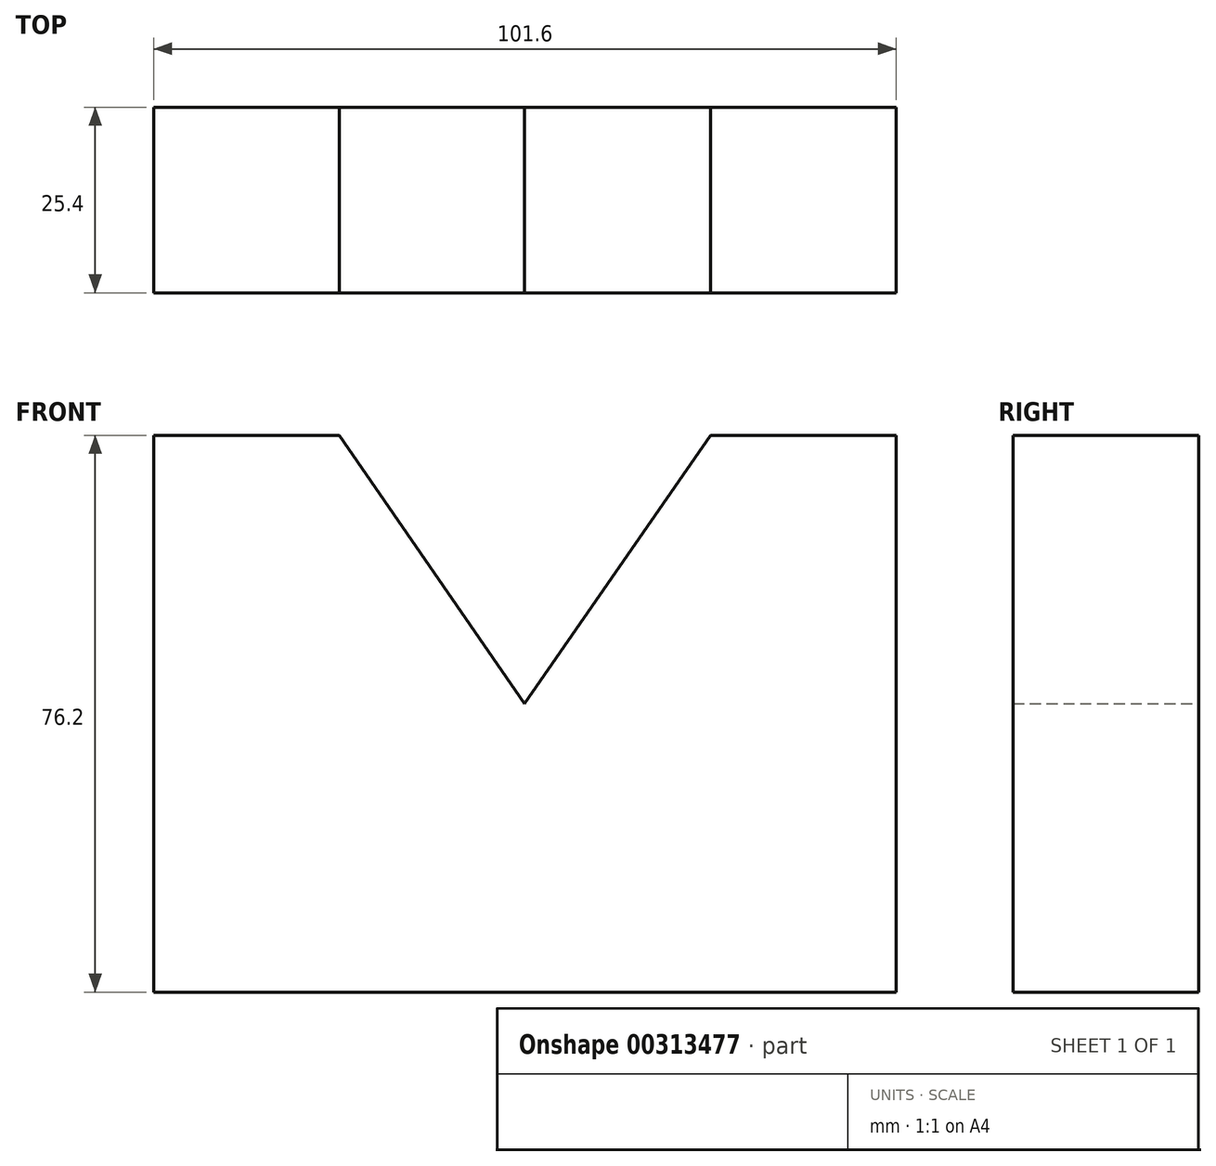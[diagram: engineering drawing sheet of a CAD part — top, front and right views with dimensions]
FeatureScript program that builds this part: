
annotation { "Feature Type Name" : "Feature", "Feature Type Description" : "" }
export const myFeature = defineFeature(function(context is Context, id is Id, definition is map)
    precondition{}
    {
        {
            var Q0;
            Q0=qCreatedBy(makeId("Front.planeOp"),FACE);
            var sketch = newSketch(context, id + "F0", { "sketchPlane" : qUnion([Q0])});
            skLineSegment(sketch, "E0", {"start": v(-38.6, -40.62) * mm, "end": v(63, -40.62) * mm});
            skLineSegment(sketch, "E1", {"start": v(-38.6, -40.62) * mm, "end": v(-38.6, 35.58) * mm});
            skLineSegment(sketch, "E2", {"start": v(63, -40.62) * mm, "end": v(63, 35.58) * mm});
            skLineSegment(sketch, "E3", {"start": v(63, 35.58) * mm, "end": v(37.6, 35.58) * mm});
            skLineSegment(sketch, "E4", {"start": v(-38.6, 35.58) * mm, "end": v(-13.2, 35.58) * mm});
            skLineSegment(sketch, "E5", {"start": v(-13.2, 35.58) * mm, "end": v(12.17, -1.18) * mm});
            skLineSegment(sketch, "E6", {"start": v(37.6, 35.58) * mm, "end": v(12.17, -1.18) * mm});
            skSolve(sketch);
        }
        {
            var Q0;
            Q0 = qSketchRegion(id + "F0", true);
            extrude(context, id + "F1", {"entities" : qUnion([Q0]), "depth" : 25.4 * mm});
        }
    });
